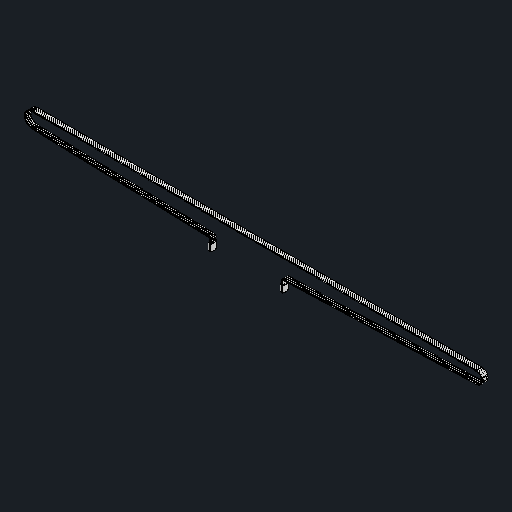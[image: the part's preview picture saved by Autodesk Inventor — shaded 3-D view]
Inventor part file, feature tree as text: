
AUTODESK INVENTOR PART (.ipt)
format: ipt  version: 2024.2 (Build 282272000, 272)  size: 1,991,168 bytes
history: native  units: mm
features: other x4, boolean_combine x1, mirror x1
ambient origin geometry x8: Origin, YZ Plane, XZ Plane, XY Plane, X Axis, Y Axis, Z Axis, Center Point
bodies: Body1 (feature_tree), Body2 (feature_tree), Body3 (feature_tree)
feature tree (6):
  other  "솔리드1"
  other  "솔리드2"
  other  "솔리드3"
  boolean_combine  "Combine1"
  other  "_belt-crimp-ndr_-_Stock-y-axis-belt-ndr-1_"
  mirror  "Mirror1"
